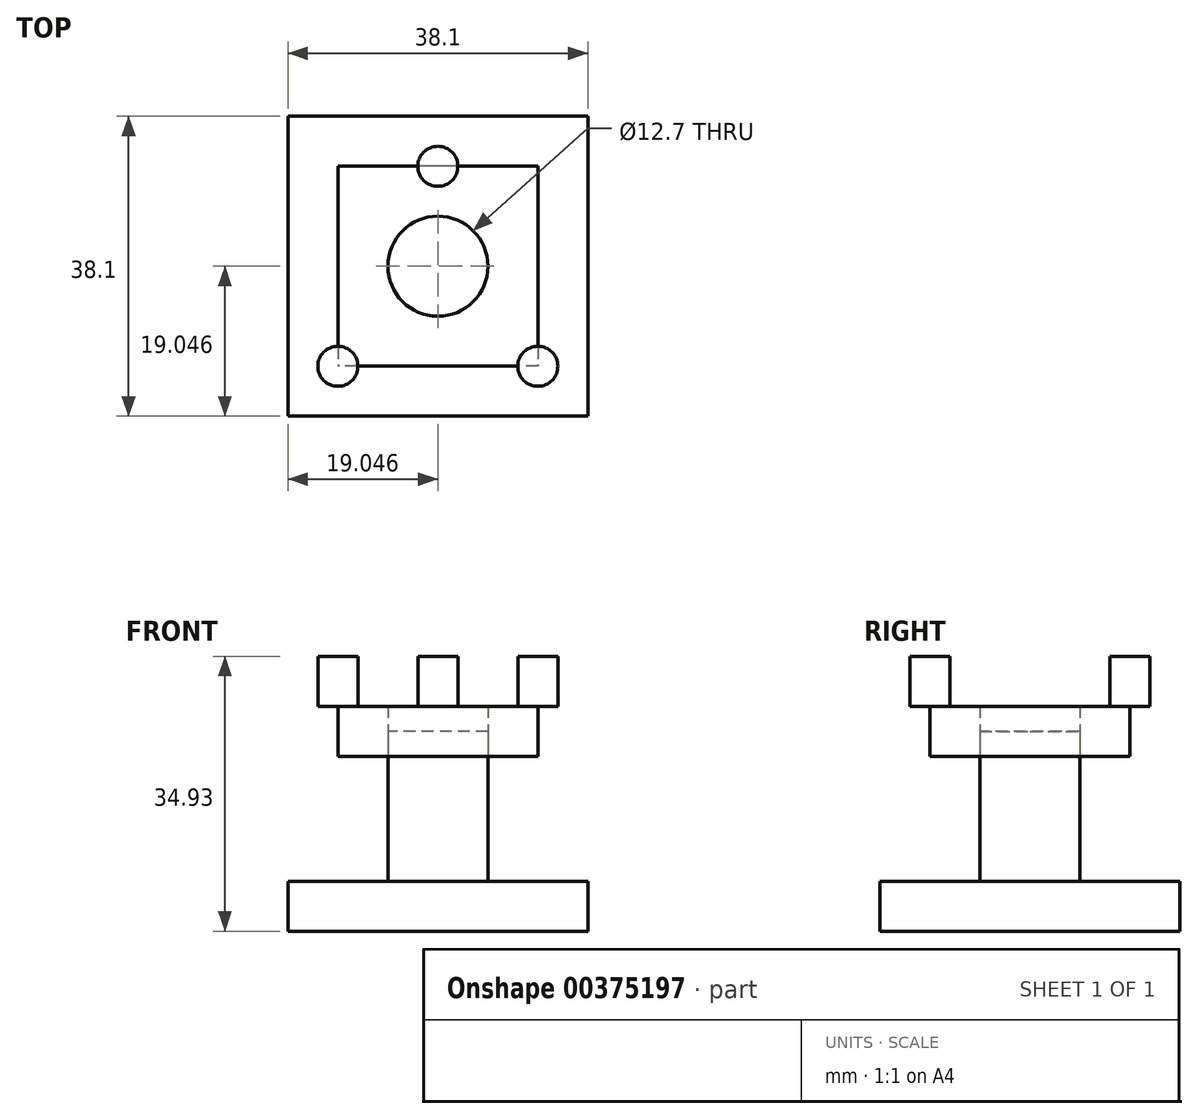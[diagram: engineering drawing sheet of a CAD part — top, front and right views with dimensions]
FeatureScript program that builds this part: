
annotation { "Feature Type Name" : "Feature", "Feature Type Description" : "" }
export const myFeature = defineFeature(function(context is Context, id is Id, definition is map)
    precondition{}
    {
        {
            var Q0;
            Q0=qCreatedBy(makeId("Top.planeOp"),FACE);
            var sketch = newSketch(context, id + "F0", { "sketchPlane" : qUnion([Q0])});
            skLineSegment(sketch, "E0.bottom", {"start": v(21.34, 17.53) * mm, "end": v(-16.76, 17.53) * mm});
            skLineSegment(sketch, "E0.top", {"start": v(21.34, -20.57) * mm, "end": v(-16.76, -20.57) * mm});
            skLineSegment(sketch, "E0.left", {"start": v(21.34, 17.53) * mm, "end": v(21.34, -20.57) * mm});
            skLineSegment(sketch, "E0.right", {"start": v(-16.76, 17.53) * mm, "end": v(-16.76, -20.57) * mm});
            skPoint(sketch, "E0.middle", {"position": v(2.29, -1.52) * mm});
            skSolve(sketch);
        }
        {
            var Q0;
            Q0=makeQuery(id+"F0.imprint","IMPRINT",FACE,{"disambiguationData":[TD([[makeQuery(id+"F0.imprint","IMPRINT",EDGE,{"derivedFrom":sQuery(id+"F0.wireOp",EDGE,"E0.bottom")}),1.0]])]});
            extrude(context, id + "F1", {"entities" : qUnion([Q0]), "depth" : 6.35 * mm});
        }
        {
            var Q0;
            Q0=makeQuery(id+"F1.opExtrude","CAP_FACE",FACE,{"disambiguationData":[OSD([sQuery(id+"F0.wireOp",EDGE,"E0.bottom"),sQuery(id+"F0.wireOp",EDGE,"E0.top"),sQuery(id+"F0.wireOp",EDGE,"E0.left"),sQuery(id+"F0.wireOp",EDGE,"E0.right")])],"isStart":false});
            var sketch = newSketch(context, id + "F2", { "sketchPlane" : qUnion([Q0])});
            skCircle(sketch, "E1", {"center": v(2.29, -1.52) * mm, "radius": 6.35 * mm});
            skPoint(sketch, "E1.centerSnap0", {"position": v(21.34, -1.52) * mm});
            skPoint(sketch, "E1.centerSnap1", {"position": v(2.29, -20.57) * mm});
            skSolve(sketch);
        }
        {
            var Q0;
            Q0 = qSketchRegion(id + "F2", true);
            extrude(context, id + "F3", {"entities" : qUnion([Q0]), "operationType" : NewBodyOperationType.ADD, "depth" : 19.05 * mm});
        }
        {
            var Q0;
            Q0=makeQuery(id+"F3.opExtrude","CAP_FACE",FACE,{"disambiguationData":[OSD([sQuery(id+"F2.wireOp",EDGE,"E1")])],"isStart":false});
            var sketch = newSketch(context, id + "F4", { "sketchPlane" : qUnion([Q0])});
            skLineSegment(sketch, "E2.bottom", {"start": v(14.99, 11.18) * mm, "end": v(-10.41, 11.18) * mm});
            skLineSegment(sketch, "E2.top", {"start": v(14.99, -14.22) * mm, "end": v(-10.41, -14.22) * mm});
            skLineSegment(sketch, "E2.left", {"start": v(14.99, 11.18) * mm, "end": v(14.99, -14.22) * mm});
            skLineSegment(sketch, "E2.right", {"start": v(-10.41, 11.18) * mm, "end": v(-10.41, -14.22) * mm});
            skPoint(sketch, "E2.middle", {"position": v(2.29, -1.52) * mm});
            skSolve(sketch);
        }
        {
            var Q0;
            Q0=makeQuery(id+"F4.imprint","IMPRINT",FACE,{"disambiguationData":[TD([[makeQuery(id+"F4.imprint","IMPRINT",EDGE,{"derivedFrom":sQuery(id+"F4.wireOp",EDGE,"E2.bottom")}),1.0]])]});
            extrude(context, id + "F5", {"entities" : qUnion([Q0]), "endBound" : BoundingType.SYMMETRIC, "depth" : 6.35 * mm});
        }
        {
            var Q0;
            Q0=makeQuery(id+"F5.opExtrude","CAP_FACE",FACE,{"disambiguationData":[OSD([sQuery(id+"F2.wireOp",EDGE,"E1"),sQuery(id+"F4.wireOp",EDGE,"E2.bottom"),sQuery(id+"F4.wireOp",EDGE,"E2.top"),sQuery(id+"F4.wireOp",EDGE,"E2.left"),sQuery(id+"F4.wireOp",EDGE,"E2.right")])],"isStart":false});
            var sketch = newSketch(context, id + "F6", { "sketchPlane" : qUnion([Q0])});
            skCircle(sketch, "E3", {"center": v(-10.41, -14.22) * mm, "radius": 2.54 * mm});
            skCircle(sketch, "E4", {"center": v(14.99, -14.22) * mm, "radius": 2.54 * mm});
            skCircle(sketch, "E5", {"center": v(2.29, 11.18) * mm, "radius": 2.54 * mm});
            skSolve(sketch);
        }
        {
            var Q0;
            Q0 = qSketchRegion(id + "F6", true);
            extrude(context, id + "F7", {"entities" : qUnion([Q0]), "operationType" : NewBodyOperationType.ADD, "depth" : 6.35 * mm});
        }
    });
